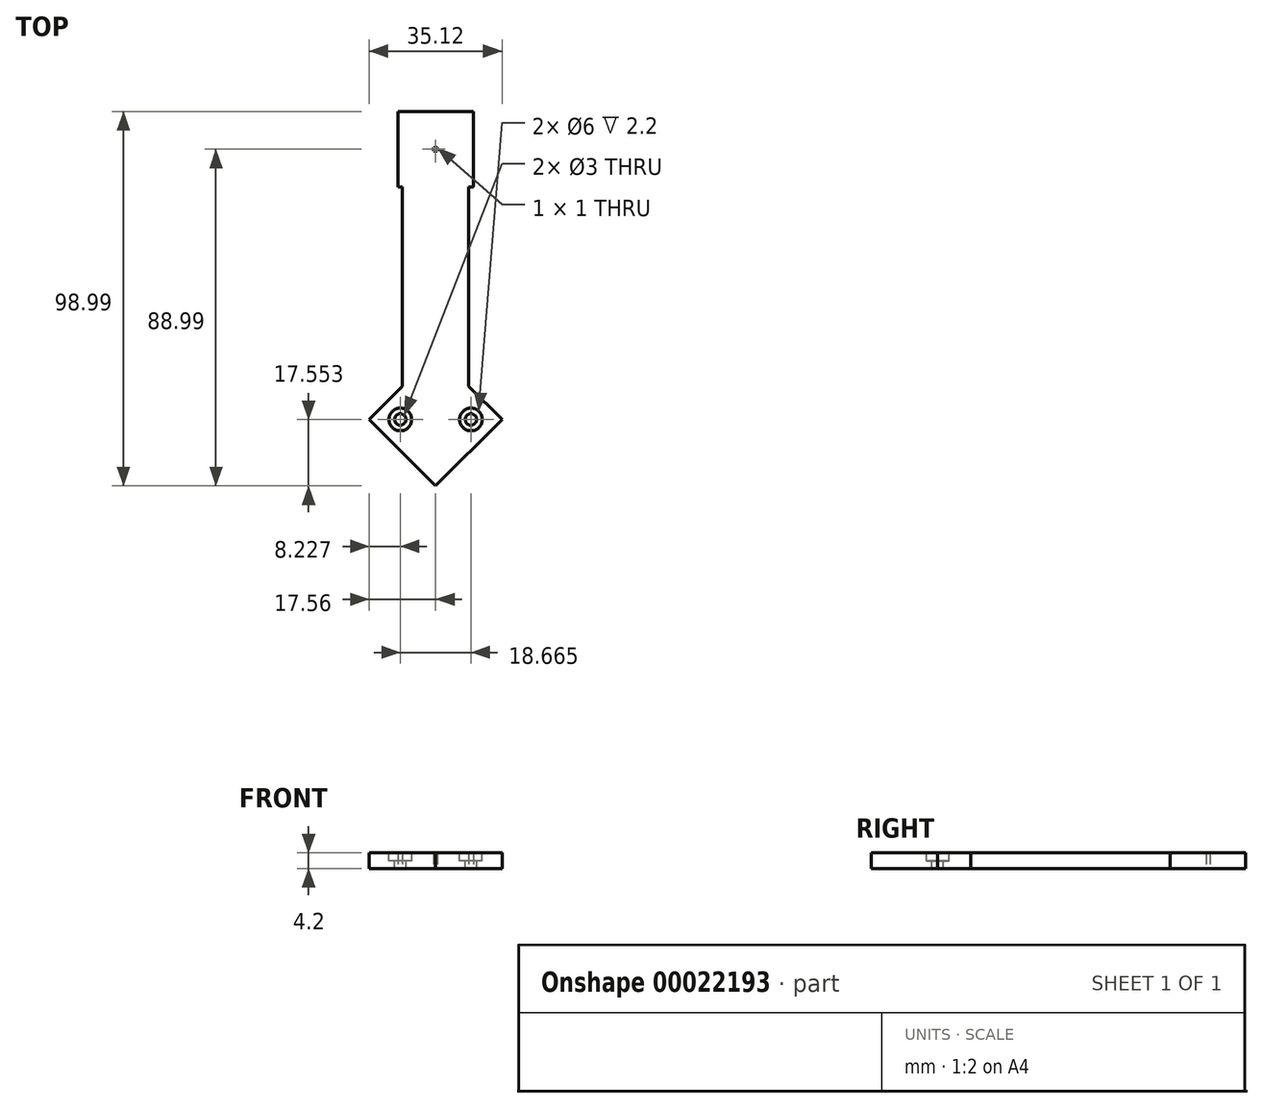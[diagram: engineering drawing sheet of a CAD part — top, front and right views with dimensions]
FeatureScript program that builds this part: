
annotation { "Feature Type Name" : "Feature", "Feature Type Description" : "" }
export const myFeature = defineFeature(function(context is Context, id is Id, definition is map)
    precondition{}
    {
        {
            var Q0;
            Q0=qCreatedBy(makeId("Top.planeOp"),FACE);
            var sketch = newSketch(context, id + "F0", { "sketchPlane" : qUnion([Q0])});
            skLineSegment(sketch, "E0.rect.bottom", {"start": v(10, 10) * mm, "end": v(-10, 10) * mm});
            skLineSegment(sketch, "E0.rect.top", {"start": v(10, -10) * mm, "end": v(-10, -10) * mm});
            skLineSegment(sketch, "E0.rect.left", {"start": v(10, 10) * mm, "end": v(10, -10) * mm});
            skLineSegment(sketch, "E0.rect.right", {"start": v(-10, 10) * mm, "end": v(-10, -10) * mm});
            skPoint(sketch, "E0.rect.middle", {"position": v(0, 0) * mm});
            skLineSegment(sketch, "E1", {"start": v(0, -53.88) * mm, "end": v(-17.56, -71.44) * mm});
            skLineSegment(sketch, "E2", {"start": v(0, -89) * mm, "end": v(-17.56, -71.44) * mm});
            skLineSegment(sketch, "E3", {"start": v(0, -53.88) * mm, "end": v(17.56, -71.44) * mm});
            skLineSegment(sketch, "E4", {"start": v(0, -89) * mm, "end": v(17.56, -71.44) * mm});
            skLineSegment(sketch, "E5", {"start": v(8.78, -62.66) * mm, "end": v(8.78, -10) * mm});
            skLineSegment(sketch, "E6", {"start": v(-8.78, -62.66) * mm, "end": v(-8.78, -10) * mm});
            skSolve(sketch);
        }
        {
            var Q0;
            Q0 = qSketchRegion(id + "F0", true);
            extrude(context, id + "F1", {"entities" : qUnion([Q0]), "depth" : 4.2 * mm});
        }
        {
            var Q0;
            Q0=makeQuery(id+"F1.opExtrude","CAP_FACE",FACE,{"disambiguationData":[OSD([sQuery(id+"F0.wireOp",EDGE,"E0.rect.bottom"),sQuery(id+"F0.wireOp",EDGE,"E0.rect.top"),sQuery(id+"F0.wireOp",EDGE,"E0.rect.left"),sQuery(id+"F0.wireOp",EDGE,"E0.rect.right"),sQuery(id+"F0.wireOp",EDGE,"E1"),sQuery(id+"F0.wireOp",EDGE,"E2"),sQuery(id+"F0.wireOp",EDGE,"E3"),sQuery(id+"F0.wireOp",EDGE,"E4"),sQuery(id+"F0.wireOp",EDGE,"E5"),sQuery(id+"F0.wireOp",EDGE,"E6")])],"isStart":false});
            var sketch = newSketch(context, id + "F2", { "sketchPlane" : qUnion([Q0])});
            skCircle(sketch, "E7", {"center": v(-9.33, -71.44) * mm, "radius": 3 * mm});
            skCircle(sketch, "E8", {"center": v(9.33, -71.44) * mm, "radius": 3 * mm});
            skLineSegment(sketch, "E9", {"start": v(-17.56, -71.44) * mm, "end": v(17.56, -71.44) * mm, "construction": true});
            skLineSegment(sketch, "E10", {"start": v(9.33, -71.44) * mm, "end": v(17.56, -71.44) * mm});
            skLineSegment(sketch, "E11", {"start": v(-9.33, -71.44) * mm, "end": v(-17.56, -71.44) * mm});
            skSolve(sketch);
        }
        {
            var Q0;
            Q0 = qSketchRegion(id + "F2", true);
            extrude(context, id + "F3", {"entities" : qUnion([Q0]), "operationType" : NewBodyOperationType.REMOVE, "oppositeDirection" : true, "depth" : 2.2 * mm});
        }
        {
            var Q0;
            Q0=makeQuery(id+"F3.boolean.opBoolean","COPY",FACE,{"derivedFrom":makeQuery(id+"F3.opExtrude","CAP_FACE",FACE,{"disambiguationData":[OSD([sQuery(id+"F2.wireOp",EDGE,"E7")])],"isStart":false})});
            var sketch = newSketch(context, id + "F4", { "sketchPlane" : qUnion([Q0])});
            skCircle(sketch, "E12", {"center": v(-9.33, -71.44) * mm, "radius": 1.5 * mm});
            skSolve(sketch);
        }
        {
            var Q0;
            Q0 = qSketchRegion(id + "F4", true);
            extrude(context, id + "F5", {"entities" : qUnion([Q0]), "operationType" : NewBodyOperationType.REMOVE, "oppositeDirection" : true, "depth" : 2 * mm});
        }
        {
            var Q0;
            Q0=makeQuery(id+"F3.boolean.opBoolean","COPY",FACE,{"derivedFrom":makeQuery(id+"F3.opExtrude","CAP_FACE",FACE,{"disambiguationData":[OSD([sQuery(id+"F2.wireOp",EDGE,"E8")])],"isStart":false})});
            var sketch = newSketch(context, id + "F6", { "sketchPlane" : qUnion([Q0])});
            skCircle(sketch, "E13", {"center": v(9.33, -71.44) * mm, "radius": 1.5 * mm});
            skSolve(sketch);
        }
        {
            var Q0;
            Q0 = qSketchRegion(id + "F6", true);
            extrude(context, id + "F7", {"entities" : qUnion([Q0]), "operationType" : NewBodyOperationType.REMOVE, "oppositeDirection" : true, "depth" : 2 * mm});
        }
        {
            var Q0;
            Q0=makeQuery(id+"F1.opExtrude","CAP_FACE",FACE,{"disambiguationData":[OSD([sQuery(id+"F0.wireOp",EDGE,"E0.rect.bottom"),sQuery(id+"F0.wireOp",EDGE,"E0.rect.top"),sQuery(id+"F0.wireOp",EDGE,"E0.rect.left"),sQuery(id+"F0.wireOp",EDGE,"E0.rect.right"),sQuery(id+"F0.wireOp",EDGE,"E1"),sQuery(id+"F0.wireOp",EDGE,"E2"),sQuery(id+"F0.wireOp",EDGE,"E3"),sQuery(id+"F0.wireOp",EDGE,"E4"),sQuery(id+"F0.wireOp",EDGE,"E5"),sQuery(id+"F0.wireOp",EDGE,"E6")])],"isStart":true});
            var sketch = newSketch(context, id + "F8", { "sketchPlane" : qUnion([Q0])});
            skLineSegment(sketch, "E14.rect.bottom", {"start": v(-0.5, 0.5) * mm, "end": v(0.5, 0.5) * mm});
            skLineSegment(sketch, "E14.rect.top", {"start": v(-0.5, -0.5) * mm, "end": v(0.5, -0.5) * mm});
            skLineSegment(sketch, "E14.rect.left", {"start": v(-0.5, 0.5) * mm, "end": v(-0.5, -0.5) * mm});
            skLineSegment(sketch, "E14.rect.right", {"start": v(0.5, 0.5) * mm, "end": v(0.5, -0.5) * mm});
            skPoint(sketch, "E14.rect.middle", {"position": v(0, 0) * mm});
            skSolve(sketch);
        }
        {
            var Q0;
            Q0 = qSketchRegion(id + "F8", true);
            extrude(context, id + "F9", {"entities" : qUnion([Q0]), "operationType" : NewBodyOperationType.REMOVE, "oppositeDirection" : true, "depth" : 4.2 * mm});
        }
    });
